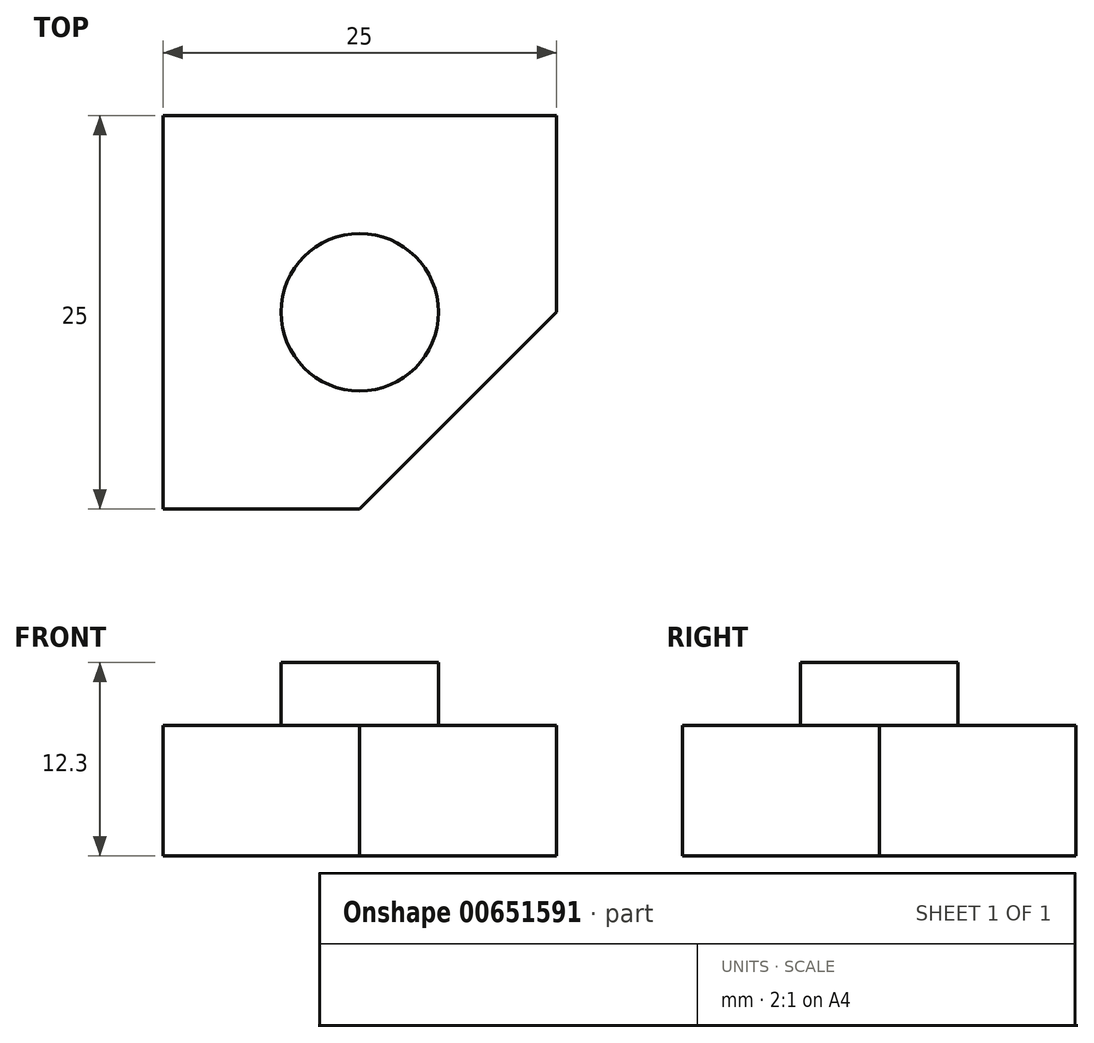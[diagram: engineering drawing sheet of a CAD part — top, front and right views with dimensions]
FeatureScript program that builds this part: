
annotation { "Feature Type Name" : "Feature", "Feature Type Description" : "" }
export const myFeature = defineFeature(function(context is Context, id is Id, definition is map)
    precondition{}
    {
        {
            var Q0;
            Q0=qCreatedBy(makeId("Top.planeOp"),FACE);
            var sketch = newSketch(context, id + "F0", { "sketchPlane" : qUnion([Q0])});
            skLineSegment(sketch, "E0.bottom", {"start": v(12.5, 12.5) * mm, "end": v(-12.5, 12.5) * mm});
            skLineSegment(sketch, "E0.top", {"start": v(12.5, -12.5) * mm, "end": v(-12.5, -12.5) * mm});
            skLineSegment(sketch, "E0.left", {"start": v(12.5, 12.5) * mm, "end": v(12.5, -12.5) * mm});
            skLineSegment(sketch, "E0.right", {"start": v(-12.5, 12.5) * mm, "end": v(-12.5, -12.5) * mm});
            skPoint(sketch, "E0.middle", {"position": v(0, 0) * mm});
            skSolve(sketch);
        }
        {
            var Q0;
            Q0=makeQuery(id+"F0.imprint","IMPRINT",FACE,{"disambiguationData":[TD([[makeQuery(id+"F0.imprint","IMPRINT",EDGE,{"derivedFrom":sQuery(id+"F0.wireOp",EDGE,"E0.bottom")}),1.0]])]});
            extrude(context, id + "F1", {"entities" : qUnion([Q0]), "depth" : 8.3 * mm});
        }
        {
            var Q0;
            Q0=makeQuery(id+"F1.opExtrude","CAP_FACE",FACE,{"disambiguationData":[OSD([sQuery(id+"F0.wireOp",EDGE,"E0.bottom"),sQuery(id+"F0.wireOp",EDGE,"E0.top"),sQuery(id+"F0.wireOp",EDGE,"E0.left"),sQuery(id+"F0.wireOp",EDGE,"E0.right")])],"isStart":false});
            var sketch = newSketch(context, id + "F2", { "sketchPlane" : qUnion([Q0])});
            skCircle(sketch, "E1", {"center": v(0, 0) * mm, "radius": 5 * mm});
            skSolve(sketch);
        }
        {
            var Q0;
            Q0=makeQuery(id+"F2.imprint","IMPRINT",FACE,{"disambiguationData":[TD([[makeQuery(id+"F2.imprint","IMPRINT",EDGE,{"derivedFrom":sQuery(id+"F2.wireOp",EDGE,"E1")}),1.0]])]});
            extrude(context, id + "F3", {"entities" : qUnion([Q0]), "operationType" : NewBodyOperationType.ADD, "depth" : 4 * mm});
        }
        {
            var Q0;
            Q0=makeQuery(id+"F1.opExtrude","CAP_FACE",FACE,{"disambiguationData":[OSD([sQuery(id+"F0.wireOp",EDGE,"E0.bottom"),sQuery(id+"F0.wireOp",EDGE,"E0.top"),sQuery(id+"F0.wireOp",EDGE,"E0.left"),sQuery(id+"F0.wireOp",EDGE,"E0.right")])],"isStart":false});
            var sketch = newSketch(context, id + "F4", { "sketchPlane" : qUnion([Q0])});
            skLineSegment(sketch, "E2", {"start": v(12.5, 0) * mm, "end": v(0, -12.5) * mm});
            skLineSegment(sketch, "E3", {"start": v(0, -12.5) * mm, "end": v(12.5, -12.5) * mm});
            skLineSegment(sketch, "E4", {"start": v(12.5, -12.5) * mm, "end": v(12.5, 0) * mm});
            skSolve(sketch);
        }
        {
            var Q0;
            Q0=makeQuery(id+"F4.imprint","IMPRINT",FACE,{"disambiguationData":[TD([[makeQuery(id+"F4.imprint","IMPRINT",EDGE,{"derivedFrom":sQuery(id+"F4.wireOp",EDGE,"E2")}),1.0]])]});
            extrude(context, id + "F5", {"entities" : qUnion([Q0]), "operationType" : NewBodyOperationType.REMOVE, "oppositeDirection" : true, "depth" : 25 * mm});
        }
    });
